# Revit family: Drain_Floor_Top_Diameter_9_Inch-Zurn-Z550-Medium-Duty
name_source: partatom
category: Plumbing Fixtures
units: mm (PartAtom-declared; Revit-internal decimal feet)

## family parameters
Always vertical = Yes
Cut with Voids When Loaded = No
Maintain Annotation Orientation = No
OmniClass Number = 23.70.50.21.24.14
OmniClass Title = Deck Waste Water Drains
Part Type = Normal
Room Calculation Point = No
Round Connector Dimension = Use Radius
Shared = No
Work Plane-Based = No

## types (22) — shared parameters
Assembly Code = D2030300
CW Connection = No
Default Elevation = 35 "
Description = 9 [229] DIAMETER TOP MEDIUM-DUTY DRAIN
Grate Open Area Sq.in = 18 "
HW Connection = No
Main Material = Iron - Zurn -Cast - Painted - Blue
Manufacturer = Zurn Water, LLC
Manufacurer Brand = Zurn
Modified Date = 09/09/2025
P Trap Primer Connetor = 0.25 "
Product Documentation Link = https://files.zurn.com
Product Page URL = https://www.zurn.com
Product data url = https://www.bimobject.com
Top Diameter Inner = 8.625 "
URL = www.zurn.com
Vent Connection = No
WFU = 1
Waste Connection = Yes
Width = 12 "
zero-valued in all types: CWFU, HWFU

## per-type parameters (varying)
| type | Approx. Weight (Lbs) | Body Height (E) | Frame Dimension | Frame and Grate | Model | Outlet Connector Radius | Pipe Size A (Actual) | Pipe Size A (Nominal) | Top Diameter | Type Comments | Z-Grate | ZN-Grate |
| Z550-2NH Outlet | 28 " | 4.75 " | 2 " | Iron - Zurn -Cast - Painted - Blue | Z550 | 1 " | 2.375 " | 2 " | 9 " | Z550-2 Inch-No Hub Outlet | Yes | No |
| Z550-2NL Outlet | 28 " | 3.5 " | 2 " | Iron - Zurn -Cast - Painted - Blue | Z550 | 1 " | 2.375 " | 2 " | 9 " | Z550-2 Inch -Neo Loc Outlet | Yes | No |
| Z550-3IC Outlet | 28 " | 3.75 " | 2 " | Iron - Zurn -Cast - Painted - Blue | Z550 | 1.5 " | 3.5 " | 3 " | 9 " | Z550-3 Inch -Inside Caulk Outlet | Yes | No |
| Z550-3IP Outlet | 28 " | 2.75 " | 2 " | Iron - Zurn -Cast - Painted - Blue | Z550 | 1.5 " | 3.5 " | 3 " | 9 " | Z550-3 Inch -Threaded Outlet | Yes | No |
| Z550-3NH Outlet | 28 " | 4.75 " | 2 " | Iron - Zurn -Cast - Painted - Blue | Z550 | 1.5 " | 3.5 " | 3 " | 9 " | Z550-3 Inch -No-Hub Outlet | Yes | No |
| Z550-3NL Outlet | 28 " | 3.5 " | 2 " | Iron - Zurn -Cast - Painted - Blue | Z550 | 1.5 " | 3.5 " | 3 " | 9 " | Z550-3 Inch -Neo-Loc Outlet | Yes | No |
| Z550-4IC Outlet | 28 " | 3.75 " | 2 " | Iron - Zurn -Cast - Painted - Blue | Z550 | 2 " | 4.5 " | 4 " | 9 " | Z550-4 Inch -Inside Caulk Outlet | Yes | No |
| Z550-4NH Outlet | 28 " | 4.75 " | 2 " | Iron - Zurn -Cast - Painted - Blue | Z550 | 2 " | 4.5 " | 4 " | 9 " | Z550-4 Inch -No-Hub Outlet | Yes | No |
| Z550-4IP Outlet | 28 " | 2.75 " | 2 " | Iron - Zurn -Cast - Painted - Blue | Z550 | 2 " | 4.5 " | 4 " | 9 " | Z550-4 Inch -Threaded Outlet | Yes | No |
| Z550-4NL Outlet | 28 " | 3.5 " | 2 " | Iron - Zurn -Cast - Painted - Blue | Z550 | 2 " | 4.5 " | 4 " | 9 " | Z550-4 Inch -Neo-Loc Outlet | Yes | No |
| Z550-6NH Outlet | 30 " | 5.25 " | 2 " | Iron - Zurn -Cast - Painted - Blue | Z550 | 3 " | 6.625 " | 6 " | 9 " | Z550-6 Inch -No Hub Outlet | Yes | No |
| ZN550-2NH Outlet | 28 " | 4.75 " | 2.188 " | Bronze - Zurn - Polished Nickel | ZN550 | 1 " | 2.375 " | 2 " | 9.75 " | ZN550-2 Inch-No Hub Outlet | No | Yes |
| ZN550-2NL Outlet | 28 " | 3.5 " | 2.188 " | Bronze - Zurn - Polished Nickel | ZN550 | 1 " | 2.375 " | 2 " | 9.75 " | ZN550-2 Inch -Neo Loc Outlet | No | Yes |
| ZN550-3IC Outlet | 28 " | 3.75 " | 2.188 " | Bronze - Zurn - Polished Nickel | ZN550 | 1.5 " | 3.5 " | 3 " | 9.75 " | ZN550-3 Inch -Inside Caulk Outlet | No | Yes |
| ZN550-3IP Outlet | 28 " | 2.75 " | 2.188 " | Bronze - Zurn - Polished Nickel | ZN550 | 1.5 " | 3.5 " | 3 " | 9.75 " | ZN550-3 Inch -Threaded Outlet | No | Yes |
| ZN550-3NH Outlet | 28 " | 4.75 " | 2.188 " | Bronze - Zurn - Polished Nickel | ZN550 | 1.5 " | 3.5 " | 3 " | 9.75 " | ZN550-3 Inch -No-Hub Outlet | No | Yes |
| ZN550-3NL Outlet | 28 " | 3.5 " | 2.188 " | Bronze - Zurn - Polished Nickel | ZN550 | 1.5 " | 3.5 " | 3 " | 9.75 " | ZN550-3 Inch -Neo-Loc Outlet | No | Yes |
| ZN550-4IC Outlet | 28 " | 3.75 " | 2.188 " | Bronze - Zurn - Polished Nickel | ZN550 | 2 " | 4.5 " | 4 " | 9.75 " | ZN550-4 Inch -Inside Caulk Outlet | No | Yes |
| ZN550-4NH Outlet | 28 " | 4.75 " | 2.188 " | Bronze - Zurn - Polished Nickel | ZN550 | 2 " | 4.5 " | 4 " | 9.75 " | ZN550-4 Inch -No-Hub Outlet | No | Yes |
| ZN550-4IP Outlet | 28 " | 2.75 " | 2.188 " | Bronze - Zurn - Polished Nickel | ZN550 | 2 " | 4.5 " | 4 " | 9.75 " | ZN550-4 Inch -Threaded Outlet | No | Yes |
| ZN550-4NL Outlet | 28 " | 3.5 " | 2.188 " | Bronze - Zurn - Polished Nickel | ZN550 | 2 " | 4.5 " | 4 " | 9.75 " | ZN550-4 Inch -Neo-Loc Outlet | No | Yes |
| ZN550-6NH Outlet | 30 " | 5.25 " | 2.188 " | Bronze - Zurn - Polished Nickel | ZN550 | 3 " | 6.625 " | 6 " | 9.75 " | ZN550-6 Inch -No Hub Outlet | No | Yes |

## geometry (parser evidence)
native form markers: Sweep x6
no freeform markers — native parametric forms only
